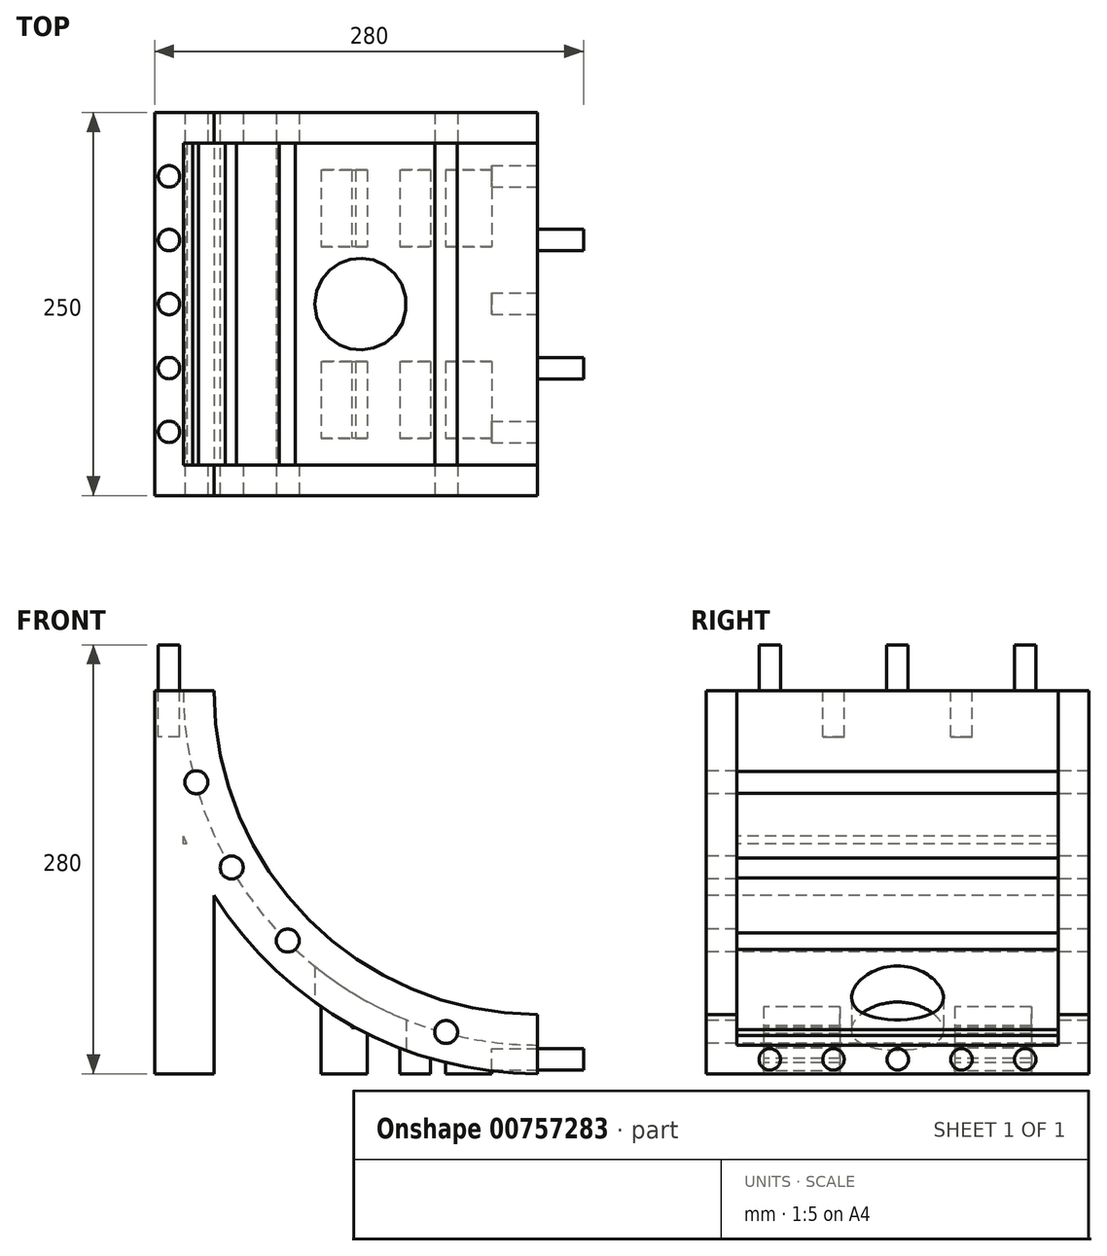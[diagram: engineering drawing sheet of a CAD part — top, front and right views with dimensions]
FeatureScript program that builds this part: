
annotation { "Feature Type Name" : "Feature", "Feature Type Description" : "" }
export const myFeature = defineFeature(function(context is Context, id is Id, definition is map)
    precondition{}
    {
        {
            var Q0;
            Q0=qCreatedBy(makeId("Front.planeOp"),FACE);
            var sketch = newSketch(context, id + "F0", { "sketchPlane" : qUnion([Q0])});
            skCircle(sketch, "E0", {"center": v(0, 0) * mm, "radius": 250 * mm});
            skLineSegment(sketch, "E1.bottom", {"start": v(250, 250) * mm, "end": v(-250, 250) * mm});
            skLineSegment(sketch, "E1.top", {"start": v(250, -250) * mm, "end": v(-250, -250) * mm});
            skLineSegment(sketch, "E1.left", {"start": v(250, 250) * mm, "end": v(250, -250) * mm});
            skLineSegment(sketch, "E1.right", {"start": v(-250, 250) * mm, "end": v(-250, -250) * mm});
            skLineSegment(sketch, "E2", {"start": v(-250, 0) * mm, "end": v(0, 0) * mm});
            skLineSegment(sketch, "E3", {"start": v(0, -250) * mm, "end": v(0, 0) * mm});
            skCircle(sketch, "E4", {"center": v(0, 0) * mm, "radius": 231.25 * mm});
            skSolve(sketch);
        }
        {
            var Q0;
            {var subQ0=sQuery(id+"F0.wireOp",EDGE,"E2");var subQ5=sQuery(id+"F0.wireOp",EDGE,"E4");var subQ6=makeQuery(id+"F0.imprint","INTERSECT",VERTEX,{"derivedFrom":[subQ0,subQ5]});Q0=makeQuery(id+"F0.imprint","IMPRINT",FACE,{"disambiguationData":[TD([[makeQuery(id+"F0.imprint","IMPRINT",EDGE,{"disambiguationData":[TD([[subQ6,-1.0]])],"derivedFrom":subQ5}),-1.0]])]});}
            extrude(context, id + "F1", {"entities" : qUnion([Q0]), "oppositeDirection" : true, "depth" : 250 * mm, "offsetDistance" : 25 * mm});
        }
        {
            var Q0;
            Q0=makeQuery(id+"F1.opExtrude","CAP_FACE",FACE,{"disambiguationData":[OSD([sQuery(id+"F0.wireOp",EDGE,"E0"),sQuery(id+"F0.wireOp",EDGE,"E2"),sQuery(id+"F0.wireOp",EDGE,"E3"),sQuery(id+"F0.wireOp",EDGE,"E4")])],"isStart":true});
            var sketch = newSketch(context, id + "F2", { "sketchPlane" : qUnion([Q0])});
            skCircle(sketch, "E5", {"center": v(0, 0) * mm, "radius": 211.25 * mm});
            skLineSegment(sketch, "E6", {"start": v(-231.25, 0) * mm, "end": v(-211.25, 0) * mm});
            skLineSegment(sketch, "E7", {"start": v(0, -231.25) * mm, "end": v(0, -211.25) * mm});
            skLineSegment(sketch, "E8", {"start": v(0, 0) * mm, "end": v(0, -250) * mm, "construction": true});
            skLineSegment(sketch, "E9", {"start": v(0, 0) * mm, "end": v(-250, 0) * mm, "construction": true});
            skSolve(sketch);
        }
        {
            var Q0;
            {var subQ0=sQuery(id+"F2.wireOp",EDGE,"E6");Q0=makeQuery(id+"F2.imprint","IMPRINT",FACE,{"disambiguationData":[TD([[makeQuery(id+"F2.imprint","IMPRINT",EDGE,{"derivedFrom":subQ0}),-1.0]])]});}
            extrude(context, id + "F3", {"entities" : qUnion([Q0]), "operationType" : NewBodyOperationType.ADD, "oppositeDirection" : true, "depth" : 20 * mm, "offsetDistance" : 25 * mm});
        }
        {
            var Q0;
            Q0=makeQuery(id+"F1.opExtrude","CAP_FACE",FACE,{"disambiguationData":[OSD([sQuery(id+"F0.wireOp",EDGE,"E0"),sQuery(id+"F0.wireOp",EDGE,"E2"),sQuery(id+"F0.wireOp",EDGE,"E3"),sQuery(id+"F0.wireOp",EDGE,"E4")])],"isStart":false});
            var sketch = newSketch(context, id + "F4", { "sketchPlane" : qUnion([Q0])});
            skCircle(sketch, "E10", {"center": v(0, 0) * mm, "radius": 211.25 * mm});
            skLineSegment(sketch, "E11", {"start": v(211.25, 0) * mm, "end": v(231.25, 0) * mm});
            skLineSegment(sketch, "E12", {"start": v(0, -211.25) * mm, "end": v(0, -231.25) * mm});
            skSolve(sketch);
        }
        {
            var Q0;
            {var subQ0=sQuery(id+"F4.wireOp",EDGE,"E11");Q0=makeQuery(id+"F4.imprint","IMPRINT",FACE,{"disambiguationData":[TD([[makeQuery(id+"F4.imprint","IMPRINT",EDGE,{"derivedFrom":subQ0}),-1.0]])]});}
            extrude(context, id + "F5", {"entities" : qUnion([Q0]), "operationType" : NewBodyOperationType.ADD, "oppositeDirection" : true, "depth" : 20 * mm, "offsetDistance" : 25 * mm});
        }
        {
            var Q0;
            {var subQ0=sQuery(id+"F0.wireOp",EDGE,"E4");Q0=makeQuery(id+"F3.boolean.opBoolean","MERGE",FACE,{"derivedFrom":[makeQuery(id+"F1.opExtrude","CAP_FACE",FACE,{"disambiguationData":[OSD([sQuery(id+"F0.wireOp",EDGE,"E0"),sQuery(id+"F0.wireOp",EDGE,"E2"),sQuery(id+"F0.wireOp",EDGE,"E3"),subQ0])],"isStart":true}),makeQuery(id+"F3.opExtrude","CAP_FACE",FACE,{"disambiguationData":[OSD([subQ0,sQuery(id+"F2.wireOp",EDGE,"E5"),sQuery(id+"F2.wireOp",EDGE,"E6"),sQuery(id+"F2.wireOp",EDGE,"E7")])],"isStart":true})]});}
            var sketch = newSketch(context, id + "F6", { "sketchPlane" : qUnion([Q0])});
            skCircle(sketch, "E13", {"center": v(0, 0) * mm, "radius": 230.62 * mm});
            skLineSegment(sketch, "E14", {"start": v(0, 0) * mm, "end": v(-250, 0) * mm, "construction": true});
            skLineSegment(sketch, "E15", {"start": v(0, 0) * mm, "end": v(0, -250) * mm, "construction": true});
            skLineSegment(sketch, "E16", {"start": v(0, 0) * mm, "end": v(-64.7, -241.48) * mm, "construction": true});
            skLineSegment(sketch, "E17", {"start": v(0, 0) * mm, "end": v(-176.78, -176.78) * mm, "construction": true});
            skLineSegment(sketch, "E18", {"start": v(0, 0) * mm, "end": v(-216.5, -125) * mm, "construction": true});
            skLineSegment(sketch, "E19", {"start": v(0, 0) * mm, "end": v(-241.48, -64.7) * mm, "construction": true});
            skLineSegment(sketch, "E20", {"start": v(0, 0) * mm, "end": v(-125, -216.5) * mm, "construction": true});
            skLineSegment(sketch, "E21", {"start": v(0, 0) * mm, "end": v(-29.4, -209.2) * mm, "construction": true});
            skPoint(sketch, "E22", {"position": v(-222.77, -59.7) * mm});
            skPoint(sketch, "E23", {"position": v(-199.73, -115.31) * mm});
            skPoint(sketch, "E24", {"position": v(-163.08, -163.08) * mm});
            skPoint(sketch, "E25", {"position": v(-115.31, -199.73) * mm});
            skPoint(sketch, "E26", {"position": v(-59.7, -222.77) * mm});
            skSolve(sketch);
        }
        {
            var Q0;
            Q0=sQuery(id+"F6.wireOp",VERTEX,"E22");
            var Q1;
            Q1=sQuery(id+"F6.wireOp",VERTEX,"E23");
            var Q2;
            Q2=sQuery(id+"F6.wireOp",VERTEX,"E24");
            var Q3;
            Q3=sQuery(id+"F6.wireOp",VERTEX,"E26");
            var Q4;
            Q4=makeQuery(id+"F1.opExtrude","SWEPT_BODY",BODY,{"disambiguationData":[OSD([sQuery(id+"F0.wireOp",EDGE,"E0"),sQuery(id+"F0.wireOp",EDGE,"E2"),sQuery(id+"F0.wireOp",EDGE,"E3"),sQuery(id+"F0.wireOp",EDGE,"E4")])]});
            hole(context, id + "F7", {"style" : HoleStyle.SIMPLE, "endStyle" : HoleEndStyle.BLIND, "holeDiameter" : 15 * mm, "majorDiameter" : 5 * mm, "holeDepth" : 400 * mm, "isTappedThrough" : true, "tappedDepth" : 12 * mm, "tapClearance" : 3, "startFromSketch" : true, "locations" : qUnion([Q0, Q1, Q2, Q3]), "scope" : qUnion([Q4])});
        }
        {
            var Q0;
            Q0=makeQuery(id+"F5.boolean.opBoolean","MERGE",FACE,{"derivedFrom":[makeQuery(id+"F3.boolean.opBoolean","MERGE",FACE,{"derivedFrom":[makeQuery(id+"F1.opExtrude","SWEPT_FACE",FACE,{"disambiguationData":[OSD([sQuery(id+"F0.wireOp",EDGE,"E3")])]}),makeQuery(id+"F3.opExtrude","SWEPT_FACE",FACE,{"disambiguationData":[OSD([sQuery(id+"F2.wireOp",EDGE,"E7")])]})]}),makeQuery(id+"F5.opExtrude","SWEPT_FACE",FACE,{"disambiguationData":[OSD([sQuery(id+"F4.wireOp",EDGE,"E12")])]})]});
            var sketch = newSketch(context, id + "F8", { "sketchPlane" : qUnion([Q0])});
            skLineSegment(sketch, "E27", {"start": v(20, -231.25) * mm, "end": v(0, -231.25) * mm, "construction": true});
            skLineSegment(sketch, "E28", {"start": v(230, -231.25) * mm, "end": v(250, -231.25) * mm, "construction": true});
            skPoint(sketch, "E28.endSnap0", {"position": v(250, -230.62) * mm});
            skLineSegment(sketch, "E29", {"start": v(41.6, -231.25) * mm, "end": v(41.6, -250) * mm, "construction": true});
            skLineSegment(sketch, "E30", {"start": v(83.2, -231.25) * mm, "end": v(83.2, -250) * mm, "construction": true});
            skLineSegment(sketch, "E31", {"start": v(125.2, -231.25) * mm, "end": v(125.2, -250) * mm, "construction": true});
            skLineSegment(sketch, "E32", {"start": v(166.8, -231.25) * mm, "end": v(166.8, -250) * mm, "construction": true});
            skLineSegment(sketch, "E33", {"start": v(208.4, -231.25) * mm, "end": v(208.4, -250) * mm, "construction": true});
            skLineSegment(sketch, "E34", {"start": v(41.6, -240.62) * mm, "end": v(83.2, -240.62) * mm, "construction": true});
            skLineSegment(sketch, "E35", {"start": v(83.2, -240.62) * mm, "end": v(125.2, -240.62) * mm, "construction": true});
            skLineSegment(sketch, "E36", {"start": v(125.2, -240.62) * mm, "end": v(166.8, -240.62) * mm, "construction": true});
            skLineSegment(sketch, "E37", {"start": v(166.8, -240.62) * mm, "end": v(208.4, -240.62) * mm, "construction": true});
            skCircle(sketch, "E38", {"center": v(41.6, -240.62) * mm, "radius": 7 * mm});
            skCircle(sketch, "E39", {"center": v(83.2, -240.62) * mm, "radius": 7 * mm});
            skCircle(sketch, "E40", {"center": v(208.4, -240.62) * mm, "radius": 7 * mm});
            skCircle(sketch, "E41", {"center": v(166.8, -240.62) * mm, "radius": 7 * mm});
            skCircle(sketch, "E42", {"center": v(125.2, -240.62) * mm, "radius": 7 * mm});
            skSolve(sketch);
        }
        {
            var Q0;
            Q0=makeQuery(id+"F8.imprint","IMPRINT",FACE,{"disambiguationData":[TD([[makeQuery(id+"F8.imprint","IMPRINT",EDGE,{"derivedFrom":sQuery(id+"F8.wireOp",EDGE,"E39")}),1.0]])]});
            var Q1;
            Q1=makeQuery(id+"F8.imprint","IMPRINT",FACE,{"disambiguationData":[TD([[makeQuery(id+"F8.imprint","IMPRINT",EDGE,{"derivedFrom":sQuery(id+"F8.wireOp",EDGE,"E41")}),1.0]])]});
            extrude(context, id + "F9", {"entities" : qUnion([Q0, Q1]), "operationType" : NewBodyOperationType.ADD, "depth" : 30 * mm, "offsetDistance" : 25 * mm});
        }
        {
            var Q0;
            Q0=makeQuery(id+"F8.imprint","IMPRINT",FACE,{"disambiguationData":[TD([[makeQuery(id+"F8.imprint","IMPRINT",EDGE,{"derivedFrom":sQuery(id+"F8.wireOp",EDGE,"E40")}),1.0]])]});
            var Q1;
            Q1=makeQuery(id+"F8.imprint","IMPRINT",FACE,{"disambiguationData":[TD([[makeQuery(id+"F8.imprint","IMPRINT",EDGE,{"derivedFrom":sQuery(id+"F8.wireOp",EDGE,"E42")}),1.0]])]});
            var Q2;
            Q2=makeQuery(id+"F8.imprint","IMPRINT",FACE,{"disambiguationData":[TD([[makeQuery(id+"F8.imprint","IMPRINT",EDGE,{"derivedFrom":sQuery(id+"F8.wireOp",EDGE,"E38")}),1.0]])]});
            extrude(context, id + "F10", {"entities" : qUnion([Q0, Q1, Q2]), "operationType" : NewBodyOperationType.REMOVE, "oppositeDirection" : true, "depth" : 30 * mm, "offsetDistance" : 25 * mm});
        }
        {
            var Q0;
            Q0=makeQuery(id+"F5.boolean.opBoolean","MERGE",FACE,{"derivedFrom":[makeQuery(id+"F3.boolean.opBoolean","MERGE",FACE,{"derivedFrom":[makeQuery(id+"F1.opExtrude","SWEPT_FACE",FACE,{"disambiguationData":[OSD([sQuery(id+"F0.wireOp",EDGE,"E2")])]}),makeQuery(id+"F3.opExtrude","SWEPT_FACE",FACE,{"disambiguationData":[OSD([sQuery(id+"F2.wireOp",EDGE,"E6")])]})]}),makeQuery(id+"F5.opExtrude","SWEPT_FACE",FACE,{"disambiguationData":[OSD([sQuery(id+"F4.wireOp",EDGE,"E11")])]})]});
            var sketch = newSketch(context, id + "F11", { "sketchPlane" : qUnion([Q0])});
            skLineSegment(sketch, "E43", {"start": v(-231.25, 230) * mm, "end": v(-250, 230) * mm, "construction": true});
            skLineSegment(sketch, "E44", {"start": v(-231.25, 20) * mm, "end": v(-250, 20) * mm, "construction": true});
            skSolve(sketch);
        }
        {
            var Q0;
            {var subQ0=sQuery(id+"F2.wireOp",EDGE,"E6");Q0=makeQuery(id+"F11.imprint","IMPRINT",FACE,{"disambiguationData":[TD([[makeQuery(id+"F11.imprint","IMPRINT",EDGE,{"derivedFrom":makeQuery(id+"F3.opExtrude","CAP_EDGE",EDGE,{"disambiguationData":[OSD([subQ0])],"isStart":false})}),-1.0]])]});}
            extrude(context, id + "F12", {"entities" : qUnion([Q0]), "operationType" : NewBodyOperationType.ADD, "oppositeDirection" : true, "depth" : 250 * mm, "offsetDistance" : 25 * mm});
        }
        {
            var Q0;
            Q0=sQuery(id+"F6.wireOp",VERTEX,"E22");
            var Q1;
            Q1=makeQuery(id+"F1.opExtrude","SWEPT_BODY",BODY,{"disambiguationData":[OSD([sQuery(id+"F0.wireOp",EDGE,"E0"),sQuery(id+"F0.wireOp",EDGE,"E2"),sQuery(id+"F0.wireOp",EDGE,"E3"),sQuery(id+"F0.wireOp",EDGE,"E4")])]});
            hole(context, id + "F13", {"style" : HoleStyle.SIMPLE, "endStyle" : HoleEndStyle.BLIND, "holeDiameter" : 15 * mm, "majorDiameter" : 5 * mm, "holeDepth" : 400 * mm, "isTappedThrough" : true, "tappedDepth" : 12 * mm, "tapClearance" : 3, "startFromSketch" : true, "locations" : qUnion([Q0]), "scope" : qUnion([Q1])});
        }
        {
            var Q0;
            Q0=makeQuery(id+"F5.boolean.opBoolean","MERGE",FACE,{"derivedFrom":[makeQuery(id+"F3.boolean.opBoolean","MERGE",FACE,{"derivedFrom":[makeQuery(id+"F1.opExtrude","SWEPT_FACE",FACE,{"disambiguationData":[OSD([sQuery(id+"F0.wireOp",EDGE,"E2")])]}),makeQuery(id+"F3.opExtrude","SWEPT_FACE",FACE,{"disambiguationData":[OSD([sQuery(id+"F2.wireOp",EDGE,"E6")])]})]}),makeQuery(id+"F5.opExtrude","SWEPT_FACE",FACE,{"disambiguationData":[OSD([sQuery(id+"F4.wireOp",EDGE,"E11")])]})]});
            var sketch = newSketch(context, id + "F14", { "sketchPlane" : qUnion([Q0])});
            skLineSegment(sketch, "E45", {"start": v(-231.25, 208.4) * mm, "end": v(-250, 208.4) * mm, "construction": true});
            skLineSegment(sketch, "E46", {"start": v(-231.25, 166.8) * mm, "end": v(-250, 166.8) * mm, "construction": true});
            skLineSegment(sketch, "E47", {"start": v(-231.25, 125.2) * mm, "end": v(-250, 125.2) * mm, "construction": true});
            skLineSegment(sketch, "E48", {"start": v(-231.25, 83.2) * mm, "end": v(-250, 83.2) * mm, "construction": true});
            skLineSegment(sketch, "E49", {"start": v(-231.25, 41.6) * mm, "end": v(-250, 41.6) * mm, "construction": true});
            skLineSegment(sketch, "E50", {"start": v(-240.62, 208.4) * mm, "end": v(-240.62, 41.6) * mm, "construction": true});
            skPoint(sketch, "E51", {"position": v(-240.62, 166.8) * mm});
            skPoint(sketch, "E52", {"position": v(-240.62, 125) * mm});
            skPoint(sketch, "E53", {"position": v(-240.62, 83.2) * mm});
            skCircle(sketch, "E54", {"center": v(-240.62, 208.4) * mm, "radius": 7 * mm});
            skCircle(sketch, "E55", {"center": v(-240.62, 166.8) * mm, "radius": 7 * mm});
            skCircle(sketch, "E56", {"center": v(-240.62, 125) * mm, "radius": 7 * mm});
            skCircle(sketch, "E57", {"center": v(-240.62, 83.2) * mm, "radius": 7 * mm});
            skCircle(sketch, "E58", {"center": v(-240.62, 41.6) * mm, "radius": 7 * mm});
            skSolve(sketch);
        }
        {
            var Q0;
            Q0=makeQuery(id+"F14.imprint","IMPRINT",FACE,{"disambiguationData":[TD([[makeQuery(id+"F14.imprint","IMPRINT",EDGE,{"derivedFrom":sQuery(id+"F14.wireOp",EDGE,"E54")}),1.0]])]});
            var Q1;
            Q1=makeQuery(id+"F14.imprint","IMPRINT",FACE,{"disambiguationData":[TD([[makeQuery(id+"F14.imprint","IMPRINT",EDGE,{"derivedFrom":sQuery(id+"F14.wireOp",EDGE,"E56")}),1.0]])]});
            var Q2;
            Q2=makeQuery(id+"F14.imprint","IMPRINT",FACE,{"disambiguationData":[TD([[makeQuery(id+"F14.imprint","IMPRINT",EDGE,{"derivedFrom":sQuery(id+"F14.wireOp",EDGE,"E58")}),1.0]])]});
            extrude(context, id + "F15", {"entities" : qUnion([Q0, Q1, Q2]), "operationType" : NewBodyOperationType.ADD, "depth" : 30 * mm, "offsetDistance" : 25 * mm});
        }
        {
            var Q0;
            Q0=makeQuery(id+"F14.imprint","IMPRINT",FACE,{"disambiguationData":[TD([[makeQuery(id+"F14.imprint","IMPRINT",EDGE,{"derivedFrom":sQuery(id+"F14.wireOp",EDGE,"E57")}),1.0]])]});
            var Q1;
            Q1=makeQuery(id+"F14.imprint","IMPRINT",FACE,{"disambiguationData":[TD([[makeQuery(id+"F14.imprint","IMPRINT",EDGE,{"derivedFrom":sQuery(id+"F14.wireOp",EDGE,"E55")}),1.0]])]});
            extrude(context, id + "F16", {"entities" : qUnion([Q0, Q1]), "operationType" : NewBodyOperationType.REMOVE, "oppositeDirection" : true, "depth" : 30 * mm, "offsetDistance" : 25 * mm});
        }
        {
            var Q0;
            Q0=makeQuery(id+"F12.opExtrude","CAP_FACE",FACE,{"disambiguationData":[OSD([sQuery(id+"F0.wireOp",EDGE,"E0"),sQuery(id+"F0.wireOp",EDGE,"E1.right"),sQuery(id+"F0.wireOp",EDGE,"E2"),sQuery(id+"F0.wireOp",EDGE,"E4"),sQuery(id+"F2.wireOp",EDGE,"E5"),sQuery(id+"F2.wireOp",EDGE,"E6"),sQuery(id+"F4.wireOp",EDGE,"E10"),sQuery(id+"F4.wireOp",EDGE,"E11")])],"isStart":false});
            var sketch = newSketch(context, id + "F17", { "sketchPlane" : qUnion([Q0])});
            skLineSegment(sketch, "E59", {"start": v(-211.25, 0) * mm, "end": v(0, 0) * mm, "construction": true});
            skLineSegment(sketch, "E60", {"start": v(-211.25, -250) * mm, "end": v(0, -250) * mm, "construction": true});
            skLineSegment(sketch, "E61", {"start": v(-231.25, -125) * mm, "end": v(0, -125) * mm, "construction": true});
            skLineSegment(sketch, "E62", {"start": v(-170, -250) * mm, "end": v(-170, 0) * mm, "construction": true});
            skLineSegment(sketch, "E63", {"start": v(-211.25, -250) * mm, "end": v(-170, -250) * mm});
            skLineSegment(sketch, "E64", {"start": v(-170, 0) * mm, "end": v(-211.25, 0) * mm});
            skLineSegment(sketch, "E65", {"start": v(-170, -250) * mm, "end": v(-170, 0) * mm});
            skLineSegment(sketch, "E66", {"start": v(-190.62, -250) * mm, "end": v(-190.62, 0) * mm});
            skLineSegment(sketch, "E67", {"start": v(-211.25, -20) * mm, "end": v(-211.25, -230) * mm});
            skLineSegment(sketch, "E68", {"start": v(-211.25, -20) * mm, "end": v(-211.25, -125) * mm, "construction": true});
            skLineSegment(sketch, "E69", {"start": v(-211.25, -125) * mm, "end": v(-211.25, -230) * mm, "construction": true});
            skLineSegment(sketch, "E70", {"start": v(-211.25, -72.5) * mm, "end": v(-18, -72.5) * mm, "construction": true});
            skLineSegment(sketch, "E71", {"start": v(-211.25, -177.5) * mm, "end": v(-18.2, -177.5) * mm, "construction": true});
            skLineSegment(sketch, "E72", {"start": v(-18, -72.5) * mm, "end": v(-18, -125) * mm, "construction": true});
            skLineSegment(sketch, "E73", {"start": v(-18, -125) * mm, "end": v(-18.2, -177.5) * mm, "construction": true});
            skLineSegment(sketch, "E74", {"start": v(-18, -98.75) * mm, "end": v(-190.62, -125) * mm, "construction": true});
            skLineSegment(sketch, "E75", {"start": v(-18.1, -151.25) * mm, "end": v(-190.62, -125) * mm, "construction": true});
            skLineSegment(sketch, "E76", {"start": v(-211.25, -72.5) * mm, "end": v(-231.25, -72.5) * mm, "construction": true});
            skLineSegment(sketch, "E77", {"start": v(-211.25, -177.5) * mm, "end": v(-231.25, -177.5) * mm, "construction": true});
            skLineSegment(sketch, "E78", {"start": v(-211.25, -72.5) * mm, "end": v(-18, -98.75) * mm});
            skLineSegment(sketch, "E79", {"start": v(-18, -98.75) * mm, "end": v(-18.1, -151.25) * mm});
            skLineSegment(sketch, "E80", {"start": v(-18.1, -151.25) * mm, "end": v(-211.25, -177.5) * mm});
            skLineSegment(sketch, "E81", {"start": v(-18, -72.5) * mm, "end": v(-211.25, -125) * mm, "construction": true});
            skLineSegment(sketch, "E82", {"start": v(-211.25, -125) * mm, "end": v(-18.2, -177.5) * mm, "construction": true});
            skLineSegment(sketch, "E83", {"start": v(-82.41, -90) * mm, "end": v(-82.41, -160) * mm, "construction": true});
            skCircle(sketch, "E84", {"center": v(-82.41, -125) * mm, "radius": 35 * mm, "construction": true});
            skCircle(sketch, "E85", {"center": v(-115.62, -125) * mm, "radius": 30 * mm});
            skSolve(sketch);
        }
        {
            var Q0;
            Q0=makeQuery(id+"F17.imprint","IMPRINT",FACE,{"disambiguationData":[TD([[makeQuery(id+"F17.imprint","IMPRINT",EDGE,{"derivedFrom":sQuery(id+"F17.wireOp",EDGE,"E67")}),-1.0]])]});
            extrude(context, id + "F18", {"entities" : qUnion([Q0]), "operationType" : NewBodyOperationType.ADD, "oppositeDirection" : true, "depth" : 150 * mm, "offsetDistance" : 25 * mm});
        }
        {
            var Q0;
            Q0=makeQuery(id+"F17.imprint","IMPRINT",FACE,{"disambiguationData":[TD([[makeQuery(id+"F17.imprint","IMPRINT",EDGE,{"derivedFrom":sQuery(id+"F17.wireOp",EDGE,"E85")}),1.0]])]});
            extrude(context, id + "F19", {"entities" : qUnion([Q0]), "operationType" : NewBodyOperationType.REMOVE, "oppositeDirection" : true, "depth" : 200 * mm, "offsetDistance" : 25 * mm});
        }
        {
            var Q0;
            {var subQ0=sQuery(id+"F4.wireOp",EDGE,"E11");var subQ1=sQuery(id+"F2.wireOp",EDGE,"E6");var subQ2=sQuery(id+"F0.wireOp",EDGE,"E4");var subQ3=sQuery(id+"F0.wireOp",EDGE,"E2");Q0=makeQuery(id+"F18.boolean.opBoolean","MERGE",FACE,{"derivedFrom":[makeQuery(id+"F12.opExtrude","CAP_FACE",FACE,{"disambiguationData":[OSD([sQuery(id+"F0.wireOp",EDGE,"E0"),sQuery(id+"F0.wireOp",EDGE,"E1.right"),subQ3,subQ2,sQuery(id+"F2.wireOp",EDGE,"E5"),subQ1,sQuery(id+"F4.wireOp",EDGE,"E10"),subQ0])],"isStart":false}),makeQuery(id+"F18.opExtrude","CAP_FACE",FACE,{"disambiguationData":[OSD([subQ3,subQ2,subQ1,subQ0,sQuery(id+"F17.wireOp",EDGE,"E67")])],"isStart":true})]});}
            var sketch = newSketch(context, id + "F20", { "sketchPlane" : qUnion([Q0])});
            skLineSegment(sketch, "E86", {"start": v(-211.25, 0) * mm, "end": v(0, 0) * mm, "construction": true});
            skLineSegment(sketch, "E87", {"start": v(-211.25, -250) * mm, "end": v(0, -250) * mm, "construction": true});
            skLineSegment(sketch, "E88", {"start": v(-211.25, -125) * mm, "end": v(0, -125) * mm, "construction": true});
            skLineSegment(sketch, "E89", {"start": v(-181.25, 0) * mm, "end": v(-181.25, -250) * mm, "construction": true});
            skLineSegment(sketch, "E90", {"start": v(-151.25, 0) * mm, "end": v(-151.25, -250) * mm, "construction": true});
            skPoint(sketch, "E91.endSnap0", {"position": v(-105.63, 0) * mm});
            skPoint(sketch, "E92", {"position": v(-211.25, -125) * mm});
            skPoint(sketch, "E93", {"position": v(0, -125) * mm});
            skLineSegment(sketch, "E94", {"start": v(-181.25, 0) * mm, "end": v(-181.25, -125) * mm});
            skLineSegment(sketch, "E95", {"start": v(-181.25, -125) * mm, "end": v(-181.25, -250) * mm});
            skLineSegment(sketch, "E96", {"start": v(-151.25, 0) * mm, "end": v(-151.25, -125) * mm});
            skLineSegment(sketch, "E97", {"start": v(-151.25, -125) * mm, "end": v(-151.25, -250) * mm});
            skLineSegment(sketch, "E98", {"start": v(-30, -250) * mm, "end": v(-30, 0) * mm});
            skLineSegment(sketch, "E99", {"start": v(-60, 0) * mm, "end": v(-60, -250) * mm});
            skLineSegment(sketch, "E100", {"start": v(-151.25, -187.5) * mm, "end": v(-60, -187.5) * mm, "construction": true});
            skLineSegment(sketch, "E101", {"start": v(-151.25, -62.5) * mm, "end": v(-60, -62.5) * mm, "construction": true});
            skLineSegment(sketch, "E102", {"start": v(-151.25, -87.5) * mm, "end": v(-60, -87.5) * mm});
            skLineSegment(sketch, "E103", {"start": v(-60, -37.5) * mm, "end": v(-151.25, -37.5) * mm});
            skLineSegment(sketch, "E104", {"start": v(-60, -162.5) * mm, "end": v(-151.25, -162.5) * mm});
            skLineSegment(sketch, "E105", {"start": v(-151.25, -212.5) * mm, "end": v(-60, -212.5) * mm});
            skLineSegment(sketch, "E106", {"start": v(-131.25, -37.5) * mm, "end": v(-131.25, -87.5) * mm});
            skLineSegment(sketch, "E107", {"start": v(-131.25, -162.5) * mm, "end": v(-131.25, -212.5) * mm});
            skLineSegment(sketch, "E108", {"start": v(-141.25, -162.5) * mm, "end": v(-141.25, -212.5) * mm});
            skLineSegment(sketch, "E109", {"start": v(-121.25, -162.5) * mm, "end": v(-121.25, -212.5) * mm});
            skLineSegment(sketch, "E110", {"start": v(-141.25, -37.5) * mm, "end": v(-141.25, -87.5) * mm});
            skLineSegment(sketch, "E111", {"start": v(-121.25, -37.5) * mm, "end": v(-121.25, -87.5) * mm});
            skLineSegment(sketch, "E112", {"start": v(-90, -37.5) * mm, "end": v(-90, -87.5) * mm});
            skLineSegment(sketch, "E113", {"start": v(-80, -37.5) * mm, "end": v(-80, -87.5) * mm});
            skLineSegment(sketch, "E114", {"start": v(-70, -37.5) * mm, "end": v(-70, -87.5) * mm});
            skLineSegment(sketch, "E115", {"start": v(-90, -162.5) * mm, "end": v(-90, -212.5) * mm});
            skLineSegment(sketch, "E116", {"start": v(-80, -162.5) * mm, "end": v(-80, -212.5) * mm});
            skLineSegment(sketch, "E117", {"start": v(-70, -162.5) * mm, "end": v(-70, -212.5) * mm});
            skLineSegment(sketch, "E118", {"start": v(-111.25, -37.5) * mm, "end": v(-111.25, -87.5) * mm});
            skLineSegment(sketch, "E119", {"start": v(-111.25, -162.5) * mm, "end": v(-111.25, -212.5) * mm});
            skLineSegment(sketch, "E120", {"start": v(-60, -37.5) * mm, "end": v(0, -37.5) * mm});
            skLineSegment(sketch, "E121", {"start": v(-60, -87.5) * mm, "end": v(0, -87.5) * mm});
            skLineSegment(sketch, "E122", {"start": v(-60, -162.5) * mm, "end": v(0, -162.5) * mm});
            skLineSegment(sketch, "E123", {"start": v(-60, -212.5) * mm, "end": v(0, -212.5) * mm});
            skLineSegment(sketch, "E124", {"start": v(-102.5, -212.5) * mm, "end": v(-102.5, -162.5) * mm});
            skLineSegment(sketch, "E125", {"start": v(-102.5, -87.5) * mm, "end": v(-102.5, -37.5) * mm});
            skSolve(sketch);
        }
        {
            var Q0;
            {var subQ0=sQuery(id+"F20.wireOp",EDGE,"E107");Q0=makeQuery(id+"F20.imprint","IMPRINT",FACE,{"disambiguationData":[TD([[makeQuery(id+"F20.imprint","IMPRINT",EDGE,{"derivedFrom":subQ0}),-1.0]])]});}
            var Q1;
            {var subQ0=sQuery(id+"F20.wireOp",EDGE,"E106");Q1=makeQuery(id+"F20.imprint","IMPRINT",FACE,{"disambiguationData":[TD([[makeQuery(id+"F20.imprint","IMPRINT",EDGE,{"derivedFrom":subQ0}),-1.0]])]});}
            extrude(context, id + "F21", {"entities" : qUnion([Q0, Q1]), "operationType" : NewBodyOperationType.ADD, "oppositeDirection" : true, "depth" : 50 * mm, "offsetDistance" : 25 * mm});
        }
        {
            var Q0;
            {var subQ0=sQuery(id+"F20.wireOp",EDGE,"E106");Q0=makeQuery(id+"F20.imprint","IMPRINT",FACE,{"disambiguationData":[TD([[makeQuery(id+"F20.imprint","IMPRINT",EDGE,{"derivedFrom":subQ0}),1.0]])]});}
            var Q1;
            {var subQ0=sQuery(id+"F20.wireOp",EDGE,"E107");Q1=makeQuery(id+"F20.imprint","IMPRINT",FACE,{"disambiguationData":[TD([[makeQuery(id+"F20.imprint","IMPRINT",EDGE,{"derivedFrom":subQ0}),1.0]])]});}
            extrude(context, id + "F22", {"entities" : qUnion([Q0, Q1]), "operationType" : NewBodyOperationType.ADD, "oppositeDirection" : true, "depth" : 40 * mm, "offsetDistance" : 25 * mm});
        }
        {
            var Q0;
            {var subQ0=sQuery(id+"F20.wireOp",EDGE,"E111");Q0=makeQuery(id+"F20.imprint","IMPRINT",FACE,{"disambiguationData":[TD([[makeQuery(id+"F20.imprint","IMPRINT",EDGE,{"derivedFrom":subQ0}),1.0]])]});}
            var Q1;
            {var subQ0=sQuery(id+"F20.wireOp",EDGE,"E109");Q1=makeQuery(id+"F20.imprint","IMPRINT",FACE,{"disambiguationData":[TD([[makeQuery(id+"F20.imprint","IMPRINT",EDGE,{"derivedFrom":subQ0}),1.0]])]});}
            extrude(context, id + "F23", {"entities" : qUnion([Q0, Q1]), "operationType" : NewBodyOperationType.ADD, "oppositeDirection" : true, "depth" : 30 * mm, "offsetDistance" : 25 * mm});
        }
        {
            var Q0;
            {var subQ0=sQuery(id+"F20.wireOp",EDGE,"E112");Q0=makeQuery(id+"F20.imprint","IMPRINT",FACE,{"disambiguationData":[TD([[makeQuery(id+"F20.imprint","IMPRINT",EDGE,{"derivedFrom":subQ0}),1.0]])]});}
            var Q1;
            {var subQ0=sQuery(id+"F20.wireOp",EDGE,"E115");Q1=makeQuery(id+"F20.imprint","IMPRINT",FACE,{"disambiguationData":[TD([[makeQuery(id+"F20.imprint","IMPRINT",EDGE,{"derivedFrom":subQ0}),1.0]])]});}
            extrude(context, id + "F24", {"entities" : qUnion([Q0, Q1]), "operationType" : NewBodyOperationType.ADD, "oppositeDirection" : true, "depth" : 20 * mm, "offsetDistance" : 25 * mm});
        }
        {
            var Q0;
            {var subQ0=sQuery(id+"F20.wireOp",EDGE,"E113");Q0=makeQuery(id+"F20.imprint","IMPRINT",FACE,{"disambiguationData":[TD([[makeQuery(id+"F20.imprint","IMPRINT",EDGE,{"derivedFrom":subQ0}),1.0]])]});}
            var Q1;
            {var subQ0=sQuery(id+"F20.wireOp",EDGE,"E116");Q1=makeQuery(id+"F20.imprint","IMPRINT",FACE,{"disambiguationData":[TD([[makeQuery(id+"F20.imprint","IMPRINT",EDGE,{"derivedFrom":subQ0}),1.0]])]});}
            extrude(context, id + "F25", {"entities" : qUnion([Q0, Q1]), "operationType" : NewBodyOperationType.ADD, "oppositeDirection" : true, "depth" : 15 * mm, "offsetDistance" : 25 * mm});
        }
        {
            var Q0;
            {var subQ0=sQuery(id+"F20.wireOp",EDGE,"E120");var subQ1=sQuery(id+"F20.wireOp",EDGE,"E98");var subQ2=makeQuery(id+"F20.imprint","INTERSECT",VERTEX,{"derivedFrom":[subQ1,subQ0]});Q0=makeQuery(id+"F20.imprint","IMPRINT",FACE,{"disambiguationData":[TD([[makeQuery(id+"F20.imprint","IMPRINT",EDGE,{"disambiguationData":[TD([[subQ2,1.0]])],"derivedFrom":subQ1}),1.0]])]});}
            var Q1;
            {var subQ0=sQuery(id+"F20.wireOp",EDGE,"E123");var subQ1=sQuery(id+"F20.wireOp",EDGE,"E98");var subQ2=makeQuery(id+"F20.imprint","INTERSECT",VERTEX,{"derivedFrom":[subQ1,subQ0]});Q1=makeQuery(id+"F20.imprint","IMPRINT",FACE,{"disambiguationData":[TD([[makeQuery(id+"F20.imprint","IMPRINT",EDGE,{"disambiguationData":[TD([[subQ2,-1.0]])],"derivedFrom":subQ1}),1.0]])]});}
            extrude(context, id + "F26", {"entities" : qUnion([Q0, Q1]), "operationType" : NewBodyOperationType.ADD, "oppositeDirection" : true, "depth" : 7.5 * mm, "offsetDistance" : 25 * mm});
        }
    });
